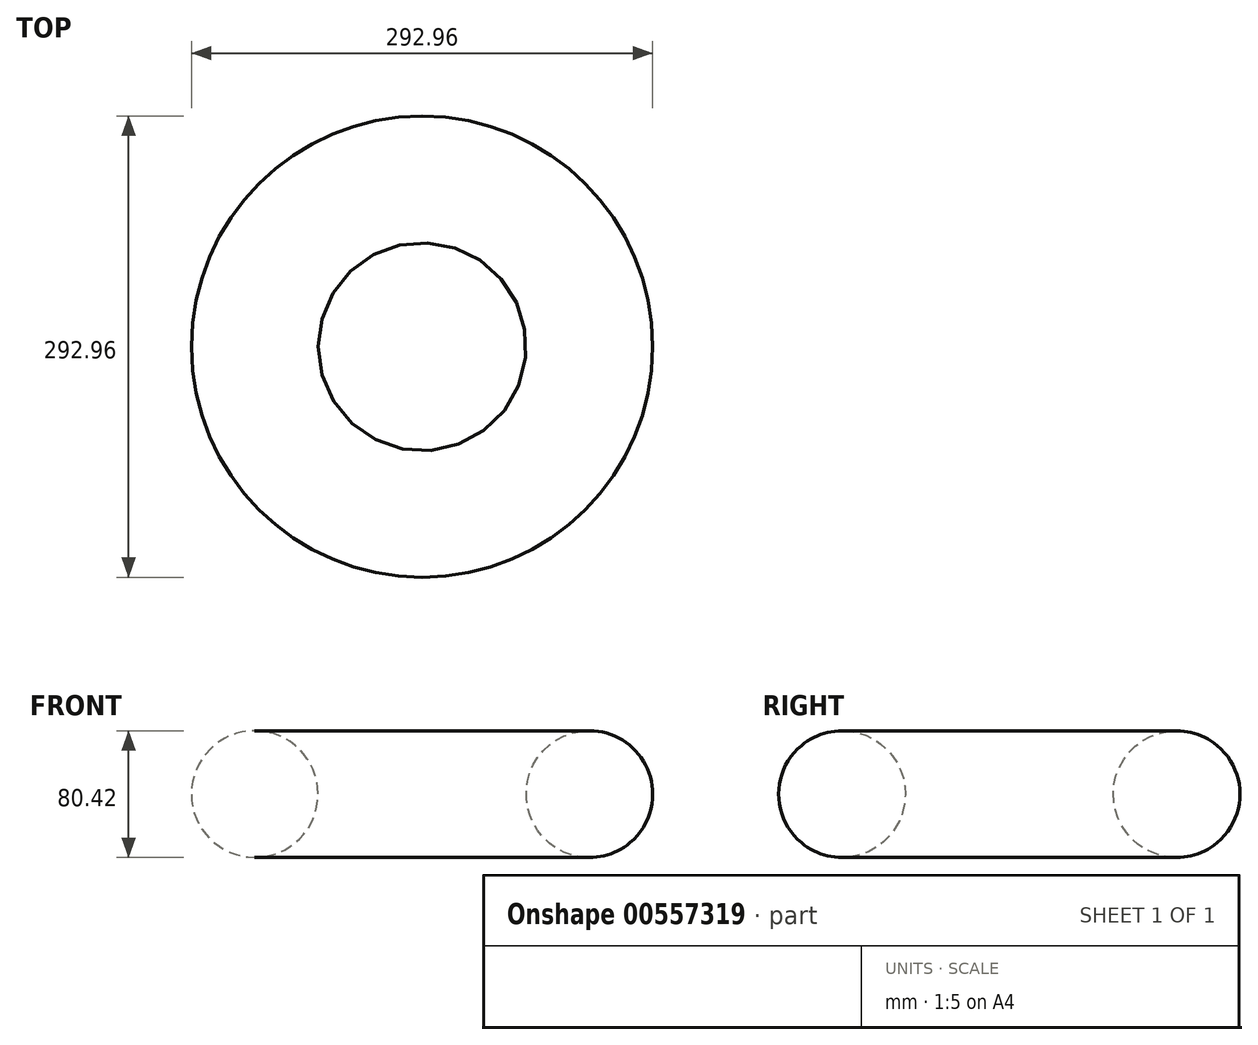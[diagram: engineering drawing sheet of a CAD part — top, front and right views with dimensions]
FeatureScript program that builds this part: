
annotation { "Feature Type Name" : "Feature", "Feature Type Description" : "" }
export const myFeature = defineFeature(function(context is Context, id is Id, definition is map)
    precondition{}
    {
        {
            var Q0;
            Q0=qCreatedBy(makeId("Front.planeOp"),FACE);
            var sketch = newSketch(context, id + "F0", { "sketchPlane" : qUnion([Q0])});
            skCircle(sketch, "E0", {"center": v(106.27, 0) * mm, "radius": 40.2 * mm});
            skSolve(sketch);
        }
        {
            var Q0;
            Q0=qCreatedBy(makeId("Front.planeOp"),FACE);
            var sketch = newSketch(context, id + "F1", { "sketchPlane" : qUnion([Q0])});
            skLineSegment(sketch, "E1", {"start": v(0, 0) * mm, "end": v(0, 108.21) * mm});
            skSolve(sketch);
        }
        {
            var Q0;
            Q0=makeQuery(id+"F0.imprint","IMPRINT",FACE,{"disambiguationData":[TD([[makeQuery(id+"F0.imprint","IMPRINT",EDGE,{"derivedFrom":sQuery(id+"F0.wireOp",EDGE,"E0")}),1.0]])]});
            var Q1;
            Q1=sQuery(id+"F1.wireOp",EDGE,"E1");
            revolve(context, id + "F2", {"entities" : qUnion([Q0]), "axis" : qUnion([Q1]), "revolveType" : RevolveType.FULL});
        }
    });
